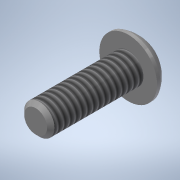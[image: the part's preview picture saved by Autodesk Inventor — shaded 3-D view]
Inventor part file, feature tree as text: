
AUTODESK INVENTOR PART (.ipt)
format: ipt  version: 2020 (Build 240168000, 168)  size: 207,360 bytes
history: native  units: in
note: dims shown in document units (in); Inventor stores cm internally (conversion verified against a paired STEP export)
features: sketch x3, extrude x2, revolve x1, chamfer x1, thread x1
ambient origin geometry x8: Origin, YZ Plane, XZ Plane, XY Plane, X Axis, Y Axis, Z Axis, Center Point
bodies: Solid1 (feature_tree)
feature tree (8):
  extrude  "Extrusion1"  Depth=0.5in TaperAngle=0.0deg
  revolve  "Revolution1"  [1 undecoded]
  extrude  "Extrusion2"  Depth=0.0938in
  chamfer  "Chamfer1"  Distance=0.0625in
  thread  "Thread1"  [1 undecoded]
  sketch  "Sketch1"  dims[d0=0.164in d1=0.5in d2=0.0in]
  sketch  "Sketch2"  dims[d3=0.087in d6=0.08in]
  sketch  "Sketch3"  dims[d7=90.0deg d8=0.0938in d9=0.0625in d10=0.0in d13=0.02in d14=0.125in d15=45.0deg d16=1.0in d17=0.0in d19=0.156in]
note: 2 required parameter values undecoded (feature->parameter linkage not recoverable at this tier; creation-order binding heuristic only, values carry confidence <= 0.55)